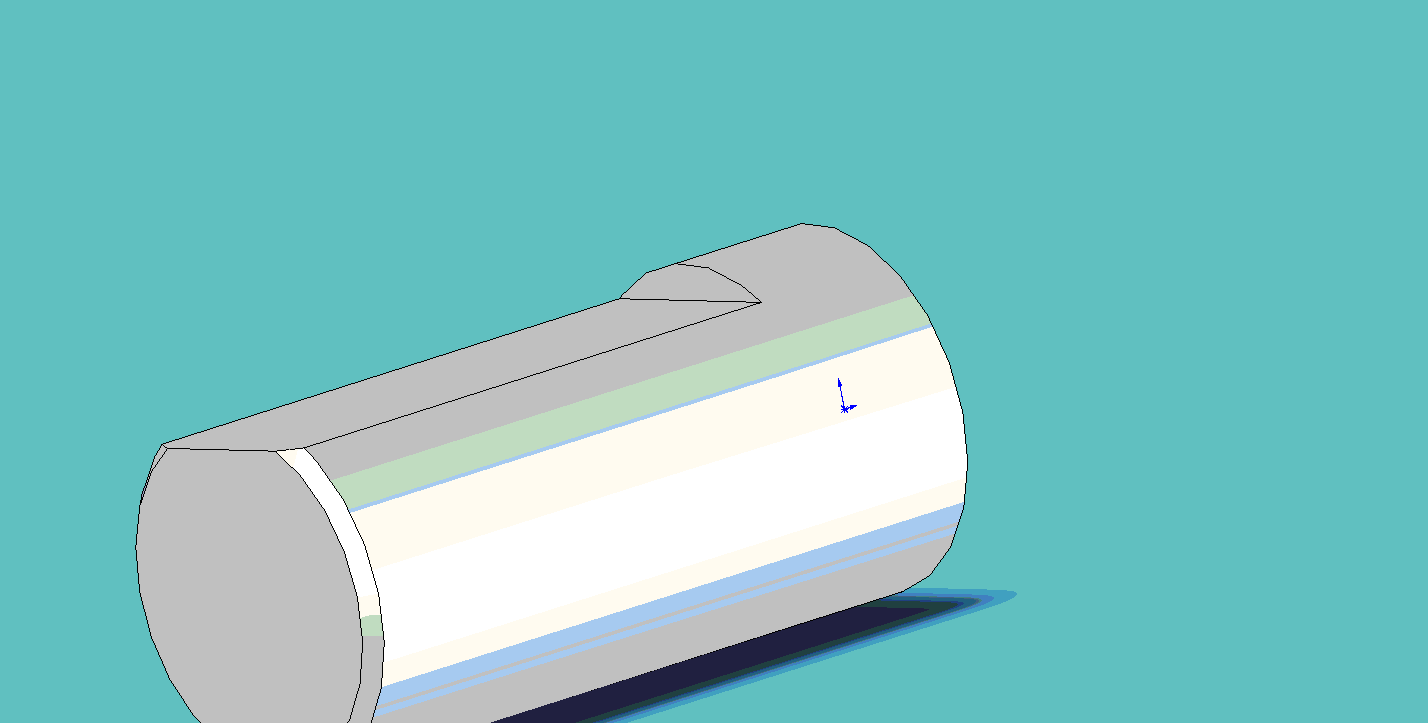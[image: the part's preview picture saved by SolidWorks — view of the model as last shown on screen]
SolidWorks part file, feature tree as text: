
SOLIDWORKS PART (.sldprt)
format: sldprt  version: not decoded by parser v0  size: 180,224 bytes
history: native  units: mm
features: plane x3, sketch x2, material x1, revolve x1, cut_extrude x1, chamfer x1 (+8 scaffold rows collapsed)
feature tree (17):
  scaffold x8  (default folders/planes/origin — collapsed)
  material  "Matériau <non spécifié>"
  plane  "Plan de face"
  plane  "Plan de dessus"
  plane  "Plan de droite"
  sketch  "Esquisse1"  dims[D1=5.0mm D2=10.15mm]
  revolve  "Révolution1"  Angle=360deg
  sketch  "Esquisse2"  dims[D1=4.5mm]
  cut_extrude  "Enlèv. mat.-Extru.1"  Depth=8mm
  chamfer  "Chanfrein1"  Distance=0.2mm Angle=45deg
decode coverage: 5 of 5 modeling features carry decoded parameters
note: suppression state not decoded; provenance and decode notes live in map.json
